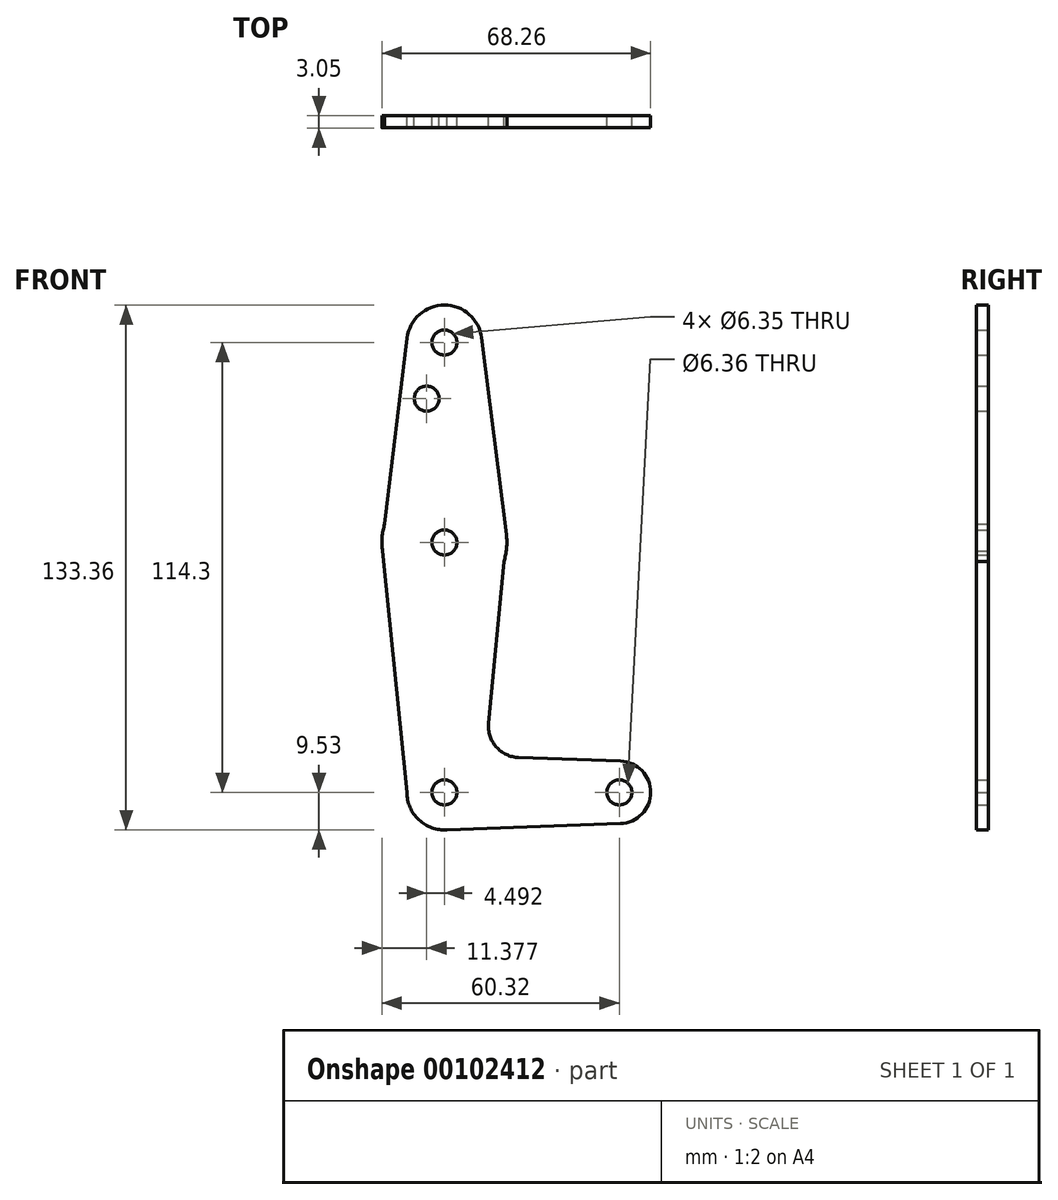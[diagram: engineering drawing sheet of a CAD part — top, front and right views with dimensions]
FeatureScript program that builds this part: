
annotation { "Feature Type Name" : "Feature", "Feature Type Description" : "" }
export const myFeature = defineFeature(function(context is Context, id is Id, definition is map)
    precondition{}
    {
        {
            var Q0;
            Q0=qCreatedBy(makeId("Front.planeOp"),FACE);
            var sketch = newSketch(context, id + "F0", { "sketchPlane" : qUnion([Q0])});
            skLineSegment(sketch, "E0", {"start": v(0, 114.3) * mm, "end": v(0, 0) * mm, "construction": true});
            skLineSegment(sketch, "E1", {"start": v(0, 0) * mm, "end": v(44.45, 0) * mm, "construction": true});
            skCircle(sketch, "E2", {"center": v(0, 114.3) * mm, "radius": 9.53 * mm});
            skCircle(sketch, "E3", {"center": v(0, 63.5) * mm, "radius": 15.88 * mm});
            skCircle(sketch, "E4", {"center": v(0, 0) * mm, "radius": 9.53 * mm});
            skCircle(sketch, "E5", {"center": v(44.45, 0) * mm, "radius": 7.94 * mm});
            skLineSegment(sketch, "E6", {"start": v(-9.46, 115.44) * mm, "end": v(-15.85, 62.54) * mm});
            skLineSegment(sketch, "E7", {"start": v(9.45, 115.5) * mm, "end": v(15.75, 65.48) * mm});
            skLineSegment(sketch, "E8", {"start": v(-9.52, 0) * mm, "end": v(-15.85, 62.54) * mm});
            skLineSegment(sketch, "E9", {"start": v(15.75, 65.48) * mm, "end": v(11.22, 17.55) * mm});
            skLineSegment(sketch, "E10", {"start": v(18.86, 8.85) * mm, "end": v(44.73, 7.93) * mm});
            skLineSegment(sketch, "E11", {"start": v(0, -9.53) * mm, "end": v(44.73, -7.93) * mm});
            skCircle(sketch, "E12", {"center": v(0, 63.5) * mm, "radius": 3.18 * mm});
            skCircle(sketch, "E13", {"center": v(0, 0) * mm, "radius": 3.18 * mm});
            skCircle(sketch, "E14", {"center": v(44.45, 0) * mm, "radius": 3.18 * mm});
            skCircle(sketch, "E15", {"center": v(0, 114.3) * mm, "radius": 3.18 * mm});
            skPoint(sketch, "E16.newPointA", {"position": v(9.57, 0) * mm});
            skPoint(sketch, "E16.newPointB", {"position": v(0, 9.53) * mm});
            skArc(sketch, "E16.filletArc", {"start": v(11.22, 17.55) * mm, "mid": v(13.16, 11.55) * mm, "end": v(18.86, 8.85) * mm});
            skCircle(sketch, "E17", {"center": v(-4.5, 100.03) * mm, "radius": 3.18 * mm});
            skSolve(sketch);
        }
        {
            var Q0;
            Q0 = qSketchRegion(id + "F0", true);
            extrude(context, id + "F1", {"entities" : qUnion([Q0]), "depth" : 3.05 * mm});
        }
    });
